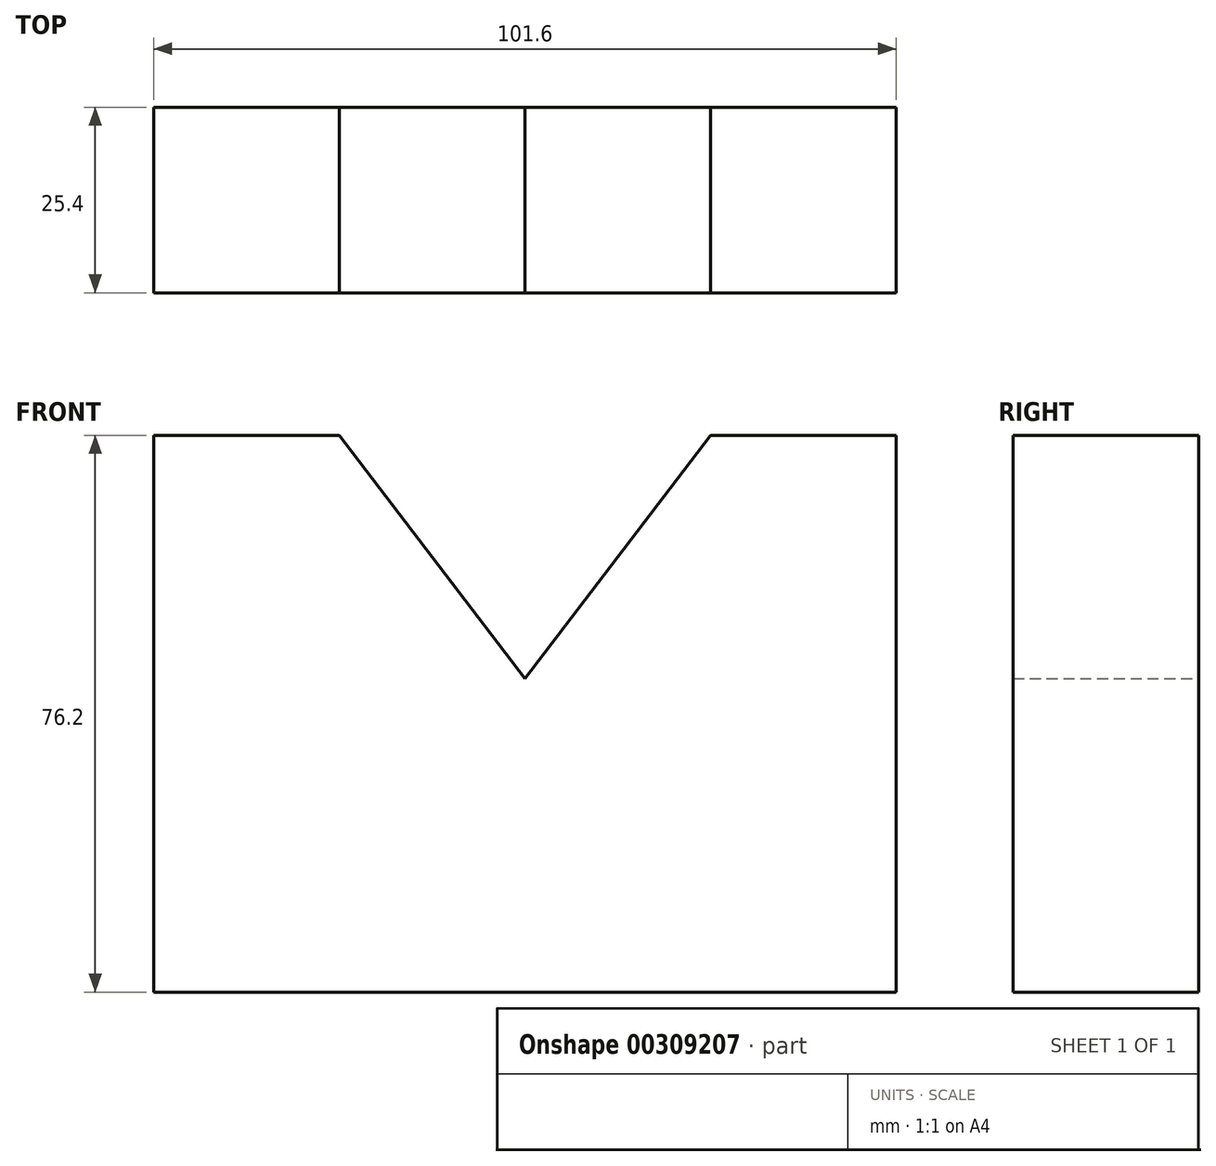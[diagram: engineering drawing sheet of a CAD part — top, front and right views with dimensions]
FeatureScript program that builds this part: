
annotation { "Feature Type Name" : "Feature", "Feature Type Description" : "" }
export const myFeature = defineFeature(function(context is Context, id is Id, definition is map)
    precondition{}
    {
        {
            var Q0;
            Q0=qCreatedBy(makeId("Front.planeOp"),FACE);
            var sketch = newSketch(context, id + "F0", { "sketchPlane" : qUnion([Q0])});
            skLineSegment(sketch, "E0", {"start": v(-47.4, -45.15) * mm, "end": v(54.2, -45.15) * mm});
            skLineSegment(sketch, "E1", {"start": v(54.2, -45.15) * mm, "end": v(54.2, 31.05) * mm});
            skLineSegment(sketch, "E2", {"start": v(-47.4, -45.15) * mm, "end": v(-47.4, 31.05) * mm});
            skLineSegment(sketch, "E3", {"start": v(-47.4, 31.05) * mm, "end": v(-22, 31.05) * mm});
            skLineSegment(sketch, "E4", {"start": v(28.8, 31.05) * mm, "end": v(54.2, 31.05) * mm});
            skPoint(sketch, "E5", {"position": v(3.4, -2.22) * mm});
            skPoint(sketch, "E5.positionSnap0", {"position": v(3.4, -45.15) * mm});
            skLineSegment(sketch, "E6", {"start": v(3.4, -2.22) * mm, "end": v(28.8, 31.05) * mm});
            skLineSegment(sketch, "E7", {"start": v(3.4, -2.22) * mm, "end": v(-22, 31.05) * mm});
            skSolve(sketch);
        }
        {
            var Q0;
            Q0=makeQuery(id+"F0.imprint","IMPRINT",FACE,{"disambiguationData":[TD([[makeQuery(id+"F0.imprint","IMPRINT",EDGE,{"derivedFrom":sQuery(id+"F0.wireOp",EDGE,"E0")}),1.0]])]});
            extrude(context, id + "F1", {"entities" : qUnion([Q0]), "depth" : 25.4 * mm});
        }
    });
